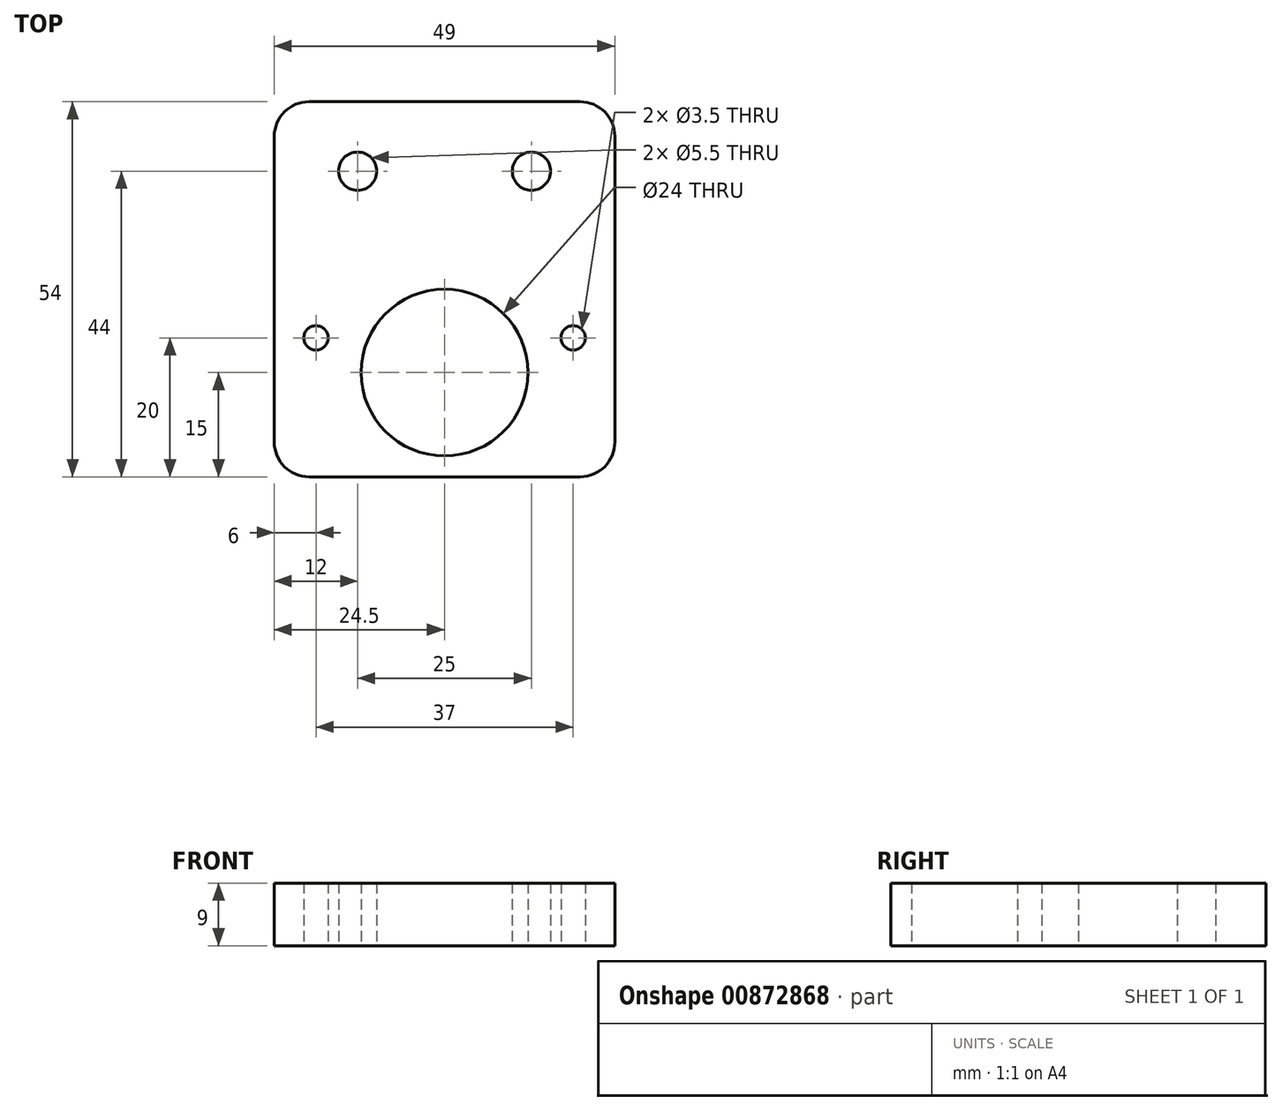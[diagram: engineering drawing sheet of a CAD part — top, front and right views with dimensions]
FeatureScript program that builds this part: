
annotation { "Feature Type Name" : "Feature", "Feature Type Description" : "" }
export const myFeature = defineFeature(function(context is Context, id is Id, definition is map)
    precondition{}
    {
        {
            var Q0;
            Q0=qCreatedBy(makeId("Top.planeOp"),FACE);
            var sketch = newSketch(context, id + "F0", { "sketchPlane" : qUnion([Q0])});
            skCircle(sketch, "E0", {"center": v(0, 0) * mm, "radius": 12 * mm});
            skCircle(sketch, "E1", {"center": v(-18.5, 5) * mm, "radius": 1.75 * mm});
            skCircle(sketch, "E2", {"center": v(18.5, 5) * mm, "radius": 1.75 * mm});
            skLineSegment(sketch, "E3.bottom", {"start": v(-19.5, 39) * mm, "end": v(19.5, 39) * mm});
            skLineSegment(sketch, "E3.top", {"start": v(-19.5, -15) * mm, "end": v(19.5, -15) * mm});
            skLineSegment(sketch, "E3.left", {"start": v(-24.5, 34) * mm, "end": v(-24.5, -10) * mm});
            skLineSegment(sketch, "E3.right", {"start": v(24.5, 34) * mm, "end": v(24.5, -10) * mm});
            skPoint(sketch, "E4.visualSharp", {"position": v(-24.5, 39) * mm});
            skArc(sketch, "E4.filletArc", {"start": v(-19.5, 39) * mm, "mid": v(-23.04, 37.54) * mm, "end": v(-24.5, 34) * mm});
            skPoint(sketch, "E5.visualSharp", {"position": v(24.5, 39) * mm});
            skArc(sketch, "E5.filletArc", {"start": v(24.5, 34) * mm, "mid": v(23.04, 37.54) * mm, "end": v(19.5, 39) * mm});
            skPoint(sketch, "E6.visualSharp", {"position": v(-24.5, -15) * mm});
            skArc(sketch, "E6.filletArc", {"start": v(-24.5, -10) * mm, "mid": v(-23.04, -13.54) * mm, "end": v(-19.5, -15) * mm});
            skPoint(sketch, "E7.visualSharp", {"position": v(24.5, -15) * mm});
            skArc(sketch, "E7.filletArc", {"start": v(19.5, -15) * mm, "mid": v(23.04, -13.54) * mm, "end": v(24.5, -10) * mm});
            skLineSegment(sketch, "E8", {"start": v(-24.5, 29) * mm, "end": v(24.5, 29) * mm, "construction": true});
            skCircle(sketch, "E9", {"center": v(-12.5, 29) * mm, "radius": 2.75 * mm});
            skCircle(sketch, "E10", {"center": v(12.5, 29) * mm, "radius": 2.75 * mm});
            skSolve(sketch);
        }
        {
            var Q0;
            Q0=makeQuery(id+"F0.imprint","IMPRINT",FACE,{"disambiguationData":[TD([[makeQuery(id+"F0.imprint","IMPRINT",EDGE,{"derivedFrom":sQuery(id+"F0.wireOp",EDGE,"E0")}),-1.0]])]});
            extrude(context, id + "F1", {"entities" : qUnion([Q0]), "depth" : 9 * mm, "offsetDistance" : 25 * mm});
        }
    });
